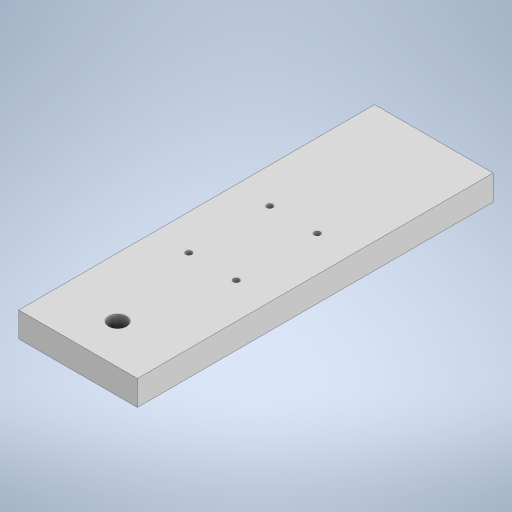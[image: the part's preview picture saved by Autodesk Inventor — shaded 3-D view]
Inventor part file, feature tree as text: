
AUTODESK INVENTOR PART (.ipt)
format: ipt  version: 2023 (Build 270158000, 158)  size: 229,376 bytes
history: native  units: in
note: dims shown in document units (in); Inventor stores cm internally (conversion verified against a paired STEP export)
features: extrude x2, sketch x2
ambient origin geometry x8: Origin, YZ Plane, XZ Plane, XY Plane, X Axis, Y Axis, Z Axis, Center Point
bodies: Solid1 (feature_tree)
feature tree (4):
  extrude  "Extrusion1"  Depth=3.5433in
  extrude  "Extrusion2"  Depth=0.3937in
  sketch  "Sketch1"  dims[d0=1.1811in d1=3.5433in]
  sketch  "Sketch2"  dims[d2=0.25in d3=0.0in d4=0.1772in d5=0.3937in d6=1.3386in d7=0.3543in d8=0.0591in d9=0.0591in d10=0.0591in d11=0.0591in d12=0.3543in d13=0.8071in d14=0.0in d15=0.0in]
